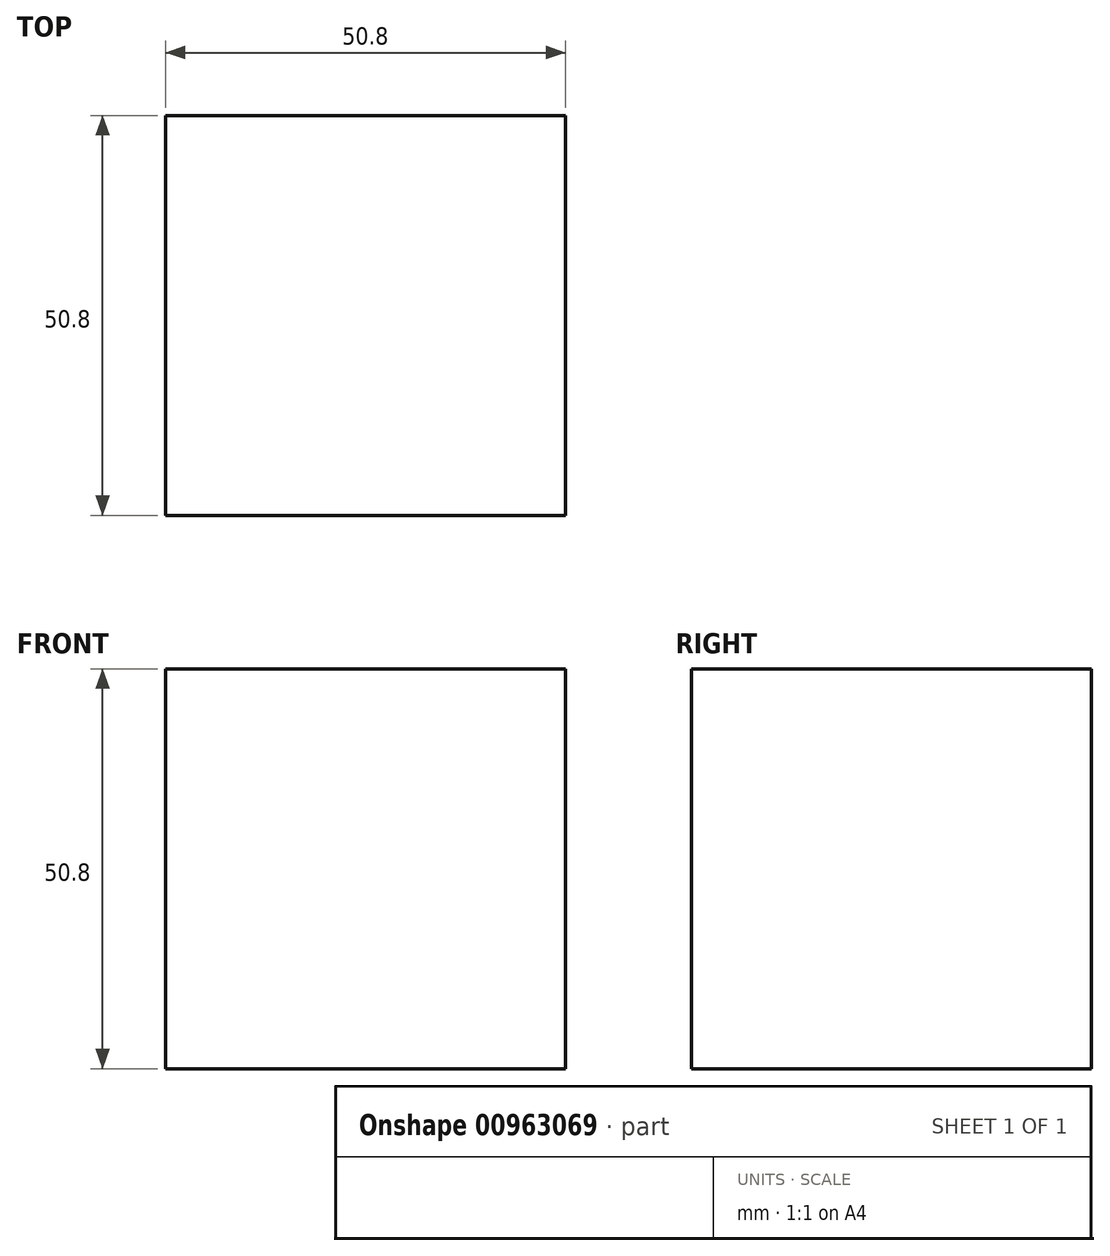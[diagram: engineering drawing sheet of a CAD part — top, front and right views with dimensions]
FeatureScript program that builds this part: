
annotation { "Feature Type Name" : "Feature", "Feature Type Description" : "" }
export const myFeature = defineFeature(function(context is Context, id is Id, definition is map)
    precondition{}
    {
        {
            var Q0;
            Q0=qCreatedBy(makeId("Front.planeOp"),FACE);
            var sketch = newSketch(context, id + "F0", { "sketchPlane" : qUnion([Q0])});
            skLineSegment(sketch, "E0.bottom", {"start": v(0, 0) * mm, "end": v(50.8, 0) * mm});
            skLineSegment(sketch, "E0.top", {"start": v(0, -50.8) * mm, "end": v(50.8, -50.8) * mm});
            skLineSegment(sketch, "E0.left", {"start": v(0, 0) * mm, "end": v(0, -50.8) * mm});
            skLineSegment(sketch, "E0.right", {"start": v(50.8, 0) * mm, "end": v(50.8, -50.8) * mm});
            skSolve(sketch);
        }
        {
            var Q0;
            Q0=makeQuery(id+"F0.imprint","IMPRINT",FACE,{"disambiguationData":[TD([[makeQuery(id+"F0.imprint","IMPRINT",EDGE,{"derivedFrom":sQuery(id+"F0.wireOp",EDGE,"E0.bottom")}),-1.0]])]});
            extrude(context, id + "F1", {"entities" : qUnion([Q0]), "depth" : 50.8 * mm, "offsetDistance" : 25.4 * mm});
        }
    });
